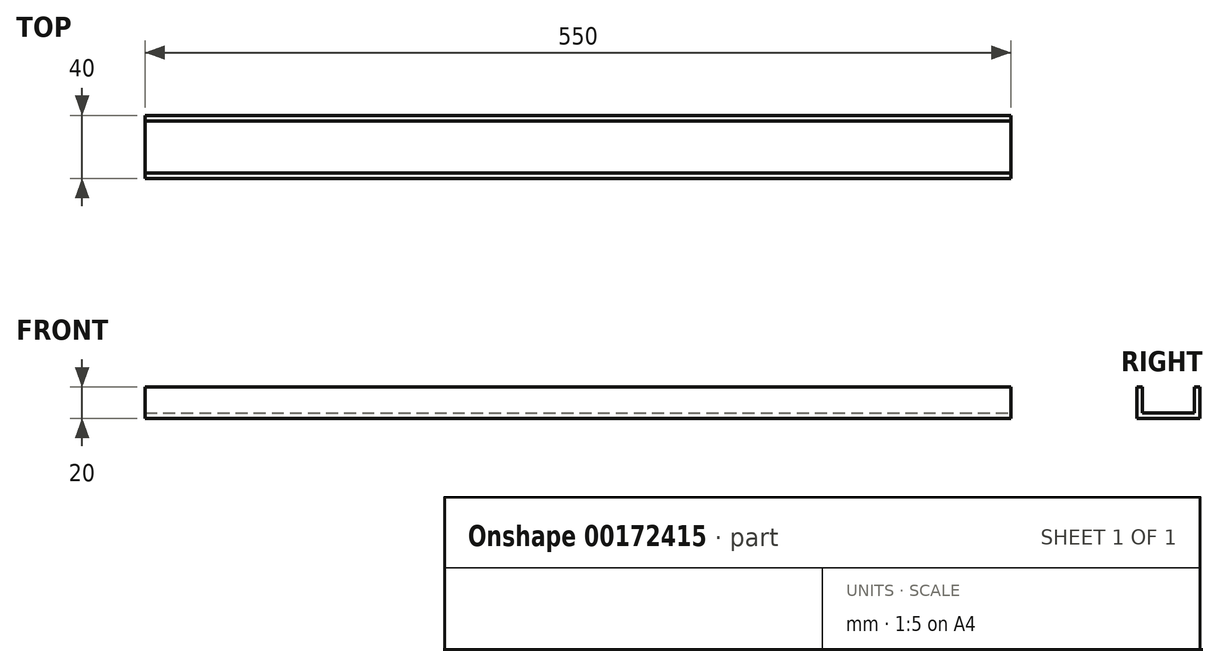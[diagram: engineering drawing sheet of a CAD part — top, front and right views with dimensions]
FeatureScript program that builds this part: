
annotation { "Feature Type Name" : "Feature", "Feature Type Description" : "" }
export const myFeature = defineFeature(function(context is Context, id is Id, definition is map)
    precondition{}
    {
        {
            var Q0;
            Q0=qCreatedBy(makeId("Top.planeOp"),FACE);
            var sketch = newSketch(context, id + "F0", { "sketchPlane" : qUnion([Q0])});
            skLineSegment(sketch, "E0.bottom", {"start": v(0, 0) * mm, "end": v(550, 0) * mm});
            skLineSegment(sketch, "E0.top", {"start": v(0, 40) * mm, "end": v(550, 40) * mm});
            skLineSegment(sketch, "E0.left", {"start": v(0, 0) * mm, "end": v(0, 40) * mm});
            skLineSegment(sketch, "E0.right", {"start": v(550, 0) * mm, "end": v(550, 40) * mm});
            skSolve(sketch);
        }
        {
            var Q0;
            Q0 = qSketchRegion(id + "F0", true);
            extrude(context, id + "F1", {"entities" : qUnion([Q0]), "depth" : 3.5 * mm});
        }
        {
            var Q0;
            Q0=makeQuery(id+"F1.opExtrude","CAP_FACE",FACE,{"disambiguationData":[OSD([sQuery(id+"F0.wireOp",EDGE,"E0.bottom"),sQuery(id+"F0.wireOp",EDGE,"E0.top"),sQuery(id+"F0.wireOp",EDGE,"E0.left"),sQuery(id+"F0.wireOp",EDGE,"E0.right")])],"isStart":false});
            var sketch = newSketch(context, id + "F2", { "sketchPlane" : qUnion([Q0])});
            skLineSegment(sketch, "E1.bottom", {"start": v(0, 0) * mm, "end": v(550, 0) * mm});
            skLineSegment(sketch, "E1.top", {"start": v(0, 3.5) * mm, "end": v(550, 3.5) * mm});
            skLineSegment(sketch, "E1.left", {"start": v(0, 0) * mm, "end": v(0, 3.5) * mm});
            skLineSegment(sketch, "E1.right", {"start": v(550, 0) * mm, "end": v(550, 3.5) * mm});
            skLineSegment(sketch, "E2.bottom", {"start": v(0, 40) * mm, "end": v(550, 40) * mm});
            skLineSegment(sketch, "E2.top", {"start": v(0, 36.5) * mm, "end": v(550, 36.5) * mm});
            skLineSegment(sketch, "E2.left", {"start": v(0, 40) * mm, "end": v(0, 36.5) * mm});
            skLineSegment(sketch, "E2.right", {"start": v(550, 40) * mm, "end": v(550, 36.5) * mm});
            skSolve(sketch);
        }
        {
            var Q0;
            Q0 = qSketchRegion(id + "F2", true);
            extrude(context, id + "F3", {"entities" : qUnion([Q0]), "operationType" : NewBodyOperationType.ADD, "depth" : (20 - 3.5) * mm});
        }
    });
